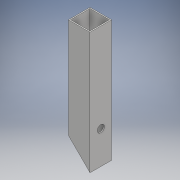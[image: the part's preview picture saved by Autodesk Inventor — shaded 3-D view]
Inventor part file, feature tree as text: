
AUTODESK INVENTOR PART (.ipt)
format: ipt  version: 2018 (Build 220112000, 112)  size: 113,664 bytes
history: native  units: mm
features: sketch x2, other x1, extrude x1, chamfer x1, hole x1
ambient origin geometry x8: Origin, YZ Plane, XZ Plane, XY Plane, X Axis, Y Axis, Z Axis, Center Point
bodies: Body1 (feature_tree)
feature tree (6):
  other  "ソリッド1"
  extrude  "押し出し1"  Depth=32.0mm
  chamfer  "面取り1"  Distance=32.0mm
  hole  "穴1"  [1 undecoded]
  sketch  "スケッチ1"
  sketch  "スケッチ2"
note: 1 required parameter value undecoded (feature->parameter linkage not recoverable at this tier; creation-order binding heuristic only, values carry confidence <= 0.55)
